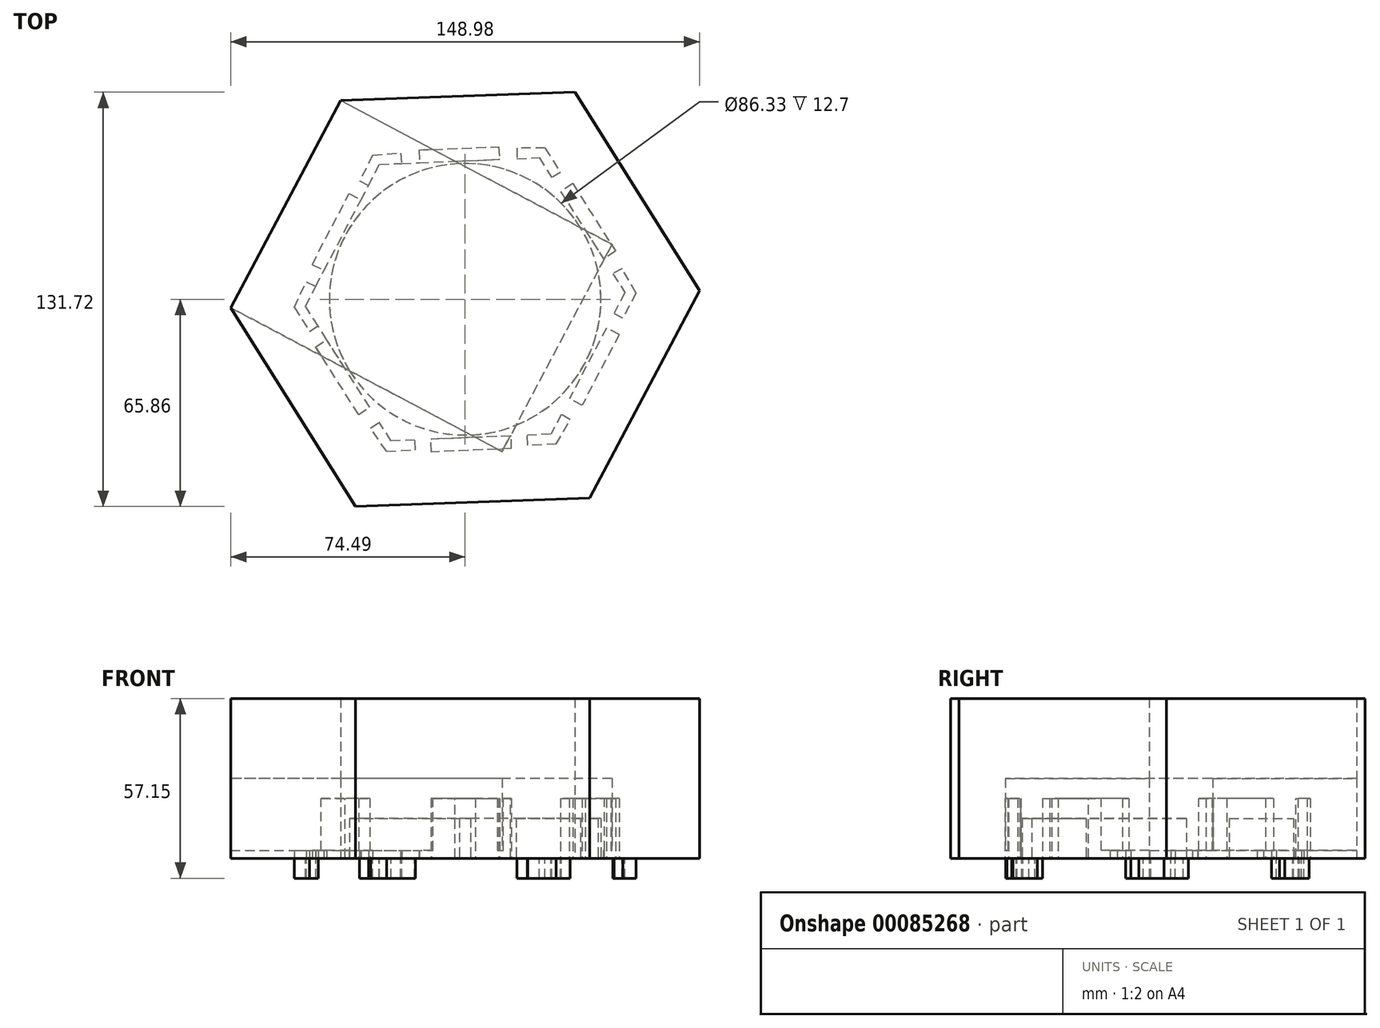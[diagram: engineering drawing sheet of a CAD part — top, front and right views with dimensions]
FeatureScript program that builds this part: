
annotation { "Feature Type Name" : "Feature", "Feature Type Description" : "" }
export const myFeature = defineFeature(function(context is Context, id is Id, definition is map)
    precondition{}
    {
        {
            var Q0;
            Q0=qCreatedBy(makeId("Top.planeOp"),FACE);
            var sketch = newSketch(context, id + "F0", { "sketchPlane" : qUnion([Q0])});
            skLineSegment(sketch, "E0.0", {"start": v(74.5, 2.7) * mm, "end": v(39.58, -63.16) * mm});
            skLineSegment(sketch, "E0.1", {"start": v(39.58, -63.16) * mm, "end": v(-34.9, -65.86) * mm});
            skLineSegment(sketch, "E0.2", {"start": v(-34.9, -65.86) * mm, "end": v(-74.5, -2.7) * mm});
            skLineSegment(sketch, "E0.3", {"start": v(-74.5, -2.7) * mm, "end": v(-39.58, 63.16) * mm});
            skLineSegment(sketch, "E0.4", {"start": v(-39.58, 63.16) * mm, "end": v(34.9, 65.86) * mm});
            skLineSegment(sketch, "E0.5", {"start": v(34.9, 65.86) * mm, "end": v(74.5, 2.7) * mm});
            skPoint(sketch, "E0.0.midPoint", {"position": v(57.04, -30.23) * mm});
            skCircle(sketch, "E1", {"center": v(0, 0) * mm, "radius": 64.56 * mm});
            skCircle(sketch, "E2", {"center": v(0, 0) * mm, "radius": 43.17 * mm});
            skSolve(sketch);
        }
        {
            var Q0;
            Q0=makeQuery(id+"F0.imprint","IMPRINT",FACE,{"disambiguationData":[TD([[makeQuery(id+"F0.imprint","IMPRINT",EDGE,{"derivedFrom":sQuery(id+"F0.wireOp",EDGE,"E0.0")}),-1.0]])]});
            var Q1;
            {var subQ0=sQuery(id+"F0.wireOp",EDGE,"E0.2");var subQ1=sQuery(id+"F0.wireOp",EDGE,"E0.1");var subQ2=makeQuery(id+"F0.imprint","INTERSECT",VERTEX,{"derivedFrom":[subQ1,subQ0]});Q1=makeQuery(id+"F0.imprint","IMPRINT",FACE,{"disambiguationData":[TD([[makeQuery(id+"F0.imprint","IMPRINT",EDGE,{"disambiguationData":[TD([[subQ2,1.0]])],"derivedFrom":subQ1}),-1.0]])]});}
            var Q2;
            {var subQ0=sQuery(id+"F0.wireOp",EDGE,"E0.3");var subQ1=sQuery(id+"F0.wireOp",EDGE,"E0.2");var subQ2=makeQuery(id+"F0.imprint","INTERSECT",VERTEX,{"derivedFrom":[subQ1,subQ0]});Q2=makeQuery(id+"F0.imprint","IMPRINT",FACE,{"disambiguationData":[TD([[makeQuery(id+"F0.imprint","IMPRINT",EDGE,{"disambiguationData":[TD([[subQ2,1.0]])],"derivedFrom":subQ1}),-1.0]])]});}
            var Q3;
            {var subQ0=sQuery(id+"F0.wireOp",EDGE,"E1");var subQ4=makeQuery(id+"F0.imprint","INTERSECT",VERTEX,{"derivedFrom":[sQuery(id+"F0.wireOp",EDGE,"E0.4"),subQ0]});Q3=makeQuery(id+"F0.imprint","IMPRINT",FACE,{"disambiguationData":[TD([[makeQuery(id+"F0.imprint","IMPRINT",EDGE,{"disambiguationData":[TD([[subQ4,1.0]])],"derivedFrom":subQ0}),1.0]])]});}
            var Q4;
            {var subQ0=sQuery(id+"F0.wireOp",EDGE,"E0.4");var subQ1=sQuery(id+"F0.wireOp",EDGE,"E0.3");var subQ2=makeQuery(id+"F0.imprint","INTERSECT",VERTEX,{"derivedFrom":[subQ1,subQ0]});Q4=makeQuery(id+"F0.imprint","IMPRINT",FACE,{"disambiguationData":[TD([[makeQuery(id+"F0.imprint","IMPRINT",EDGE,{"disambiguationData":[TD([[subQ2,1.0]])],"derivedFrom":subQ1}),-1.0]])]});}
            var Q5;
            {var subQ0=sQuery(id+"F0.wireOp",EDGE,"E0.5");var subQ1=sQuery(id+"F0.wireOp",EDGE,"E0.4");var subQ2=makeQuery(id+"F0.imprint","INTERSECT",VERTEX,{"derivedFrom":[subQ1,subQ0]});Q5=makeQuery(id+"F0.imprint","IMPRINT",FACE,{"disambiguationData":[TD([[makeQuery(id+"F0.imprint","IMPRINT",EDGE,{"disambiguationData":[TD([[subQ2,1.0]])],"derivedFrom":subQ1}),-1.0]])]});}
            var Q6;
            Q6=makeQuery(id+"F0.imprint","IMPRINT",FACE,{"disambiguationData":[TD([[makeQuery(id+"F0.imprint","IMPRINT",EDGE,{"derivedFrom":sQuery(id+"F0.wireOp",EDGE,"E2")}),1.0]])]});
            extrude(context, id + "F1", {"entities" : qUnion([Q0, Q1, Q2, Q3, Q4, Q5, Q6]), "depth" : 50.8 * mm});
        }
        {
            var Q0;
            Q0=makeQuery(id+"F0.imprint","IMPRINT",FACE,{"disambiguationData":[TD([[makeQuery(id+"F0.imprint","IMPRINT",EDGE,{"derivedFrom":sQuery(id+"F0.wireOp",EDGE,"E2")}),1.0]])]});
            extrude(context, id + "F2", {"entities" : qUnion([Q0]), "operationType" : NewBodyOperationType.REMOVE, "depth" : 12.7 * mm});
        }
        {
            var Q0;
            Q0=makeQuery(id+"F1.opExtrude","SWEPT_FACE",FACE,{"disambiguationData":[OSD([sQuery(id+"F0.wireOp",EDGE,"E0.3")])]});
            var sketch = newSketch(context, id + "F3", { "sketchPlane" : qUnion([Q0])});
            skLineSegment(sketch, "E3.bottom", {"start": v(-37.27, 25.4) * mm, "end": v(37.27, 25.4) * mm});
            skLineSegment(sketch, "E3.top", {"start": v(-37.27, 0.14) * mm, "end": v(37.27, 0.14) * mm});
            skLineSegment(sketch, "E3.left", {"start": v(-37.27, 25.4) * mm, "end": v(-37.27, 0.14) * mm});
            skLineSegment(sketch, "E3.right", {"start": v(37.27, 25.4) * mm, "end": v(37.27, 0.14) * mm});
            skPoint(sketch, "E3.middle", {"position": v(0, 12.77) * mm});
            skSolve(sketch);
        }
        {
            var Q0;
            Q0=makeQuery(id+"F0.imprint","IMPRINT",FACE,{"disambiguationData":[TD([[makeQuery(id+"F0.imprint","IMPRINT",EDGE,{"derivedFrom":sQuery(id+"F0.wireOp",EDGE,"E2")}),-1.0]])]});
            var sketch = newSketch(context, id + "F4", { "sketchPlane" : qUnion([Q0])});
            skLineSegment(sketch, "E4.0", {"start": v(-23.53, -45.02) * mm, "end": v(-50.76, -2.14) * mm});
            skLineSegment(sketch, "E4.1", {"start": v(-50.76, -2.14) * mm, "end": v(-27.23, 42.89) * mm});
            skLineSegment(sketch, "E4.2", {"start": v(-27.23, 42.89) * mm, "end": v(23.53, 45.02) * mm});
            skLineSegment(sketch, "E4.3", {"start": v(23.53, 45.02) * mm, "end": v(50.76, 2.14) * mm});
            skLineSegment(sketch, "E4.4", {"start": v(50.76, 2.14) * mm, "end": v(27.23, -42.89) * mm});
            skLineSegment(sketch, "E4.5", {"start": v(27.23, -42.89) * mm, "end": v(-23.53, -45.02) * mm});
            skPoint(sketch, "E4.0.midPoint", {"position": v(-37.14, -23.58) * mm});
            skLineSegment(sketch, "E5", {"start": v(2.02, -47.96) * mm, "end": v(-10.67, -48.5) * mm});
            skLineSegment(sketch, "E6", {"start": v(-10.67, -48.5) * mm, "end": v(-10.84, -44.49) * mm});
            skLineSegment(sketch, "E7", {"start": v(-10.84, -44.49) * mm, "end": v(14.7, -43.41) * mm});
            skLineSegment(sketch, "E8", {"start": v(2.02, -47.96) * mm, "end": v(14.7, -47.43) * mm});
            skLineSegment(sketch, "E9", {"start": v(14.7, -47.43) * mm, "end": v(14.7, -43.41) * mm});
            skLineSegment(sketch, "E10", {"start": v(43.03, -22.48) * mm, "end": v(48.91, -11.23) * mm});
            skLineSegment(sketch, "E11", {"start": v(48.91, -11.23) * mm, "end": v(44.87, -9.12) * mm});
            skLineSegment(sketch, "E12", {"start": v(43.03, -22.48) * mm, "end": v(37.15, -33.74) * mm});
            skLineSegment(sketch, "E13", {"start": v(37.15, -33.74) * mm, "end": v(33.11, -31.63) * mm});
            skLineSegment(sketch, "E14", {"start": v(-40.7, -25.84) * mm, "end": v(-33.9, -36.56) * mm});
            skLineSegment(sketch, "E15", {"start": v(-33.9, -36.56) * mm, "end": v(-30.33, -34.3) * mm});
            skLineSegment(sketch, "E16", {"start": v(-40.7, -25.84) * mm, "end": v(-47.51, -15.12) * mm});
            skLineSegment(sketch, "E17", {"start": v(-47.51, -15.12) * mm, "end": v(-43.95, -12.86) * mm});
            skPoint(sketch, "E18.start.orphan", {"position": v(39, -20.37) * mm});
            skPoint(sketch, "E19.end.orphan", {"position": v(1.85, -43.96) * mm});
            skLineSegment(sketch, "E20.MirrorCS", {"start": v(-36.85, 33.58) * mm, "end": v(-33.11, 31.63) * mm});
            skLineSegment(sketch, "E21.MirrorCS", {"start": v(-42.73, 22.33) * mm, "end": v(-36.85, 33.58) * mm});
            skLineSegment(sketch, "E22.MirrorCS", {"start": v(-42.73, 22.33) * mm, "end": v(-48.61, 11.07) * mm});
            skLineSegment(sketch, "E23.MirrorCS", {"start": v(-48.61, 11.07) * mm, "end": v(-44.87, 9.12) * mm});
            skLineSegment(sketch, "E24.MirrorCS", {"start": v(-2.02, 47.96) * mm, "end": v(10.67, 48.5) * mm});
            skLineSegment(sketch, "E25.MirrorCS", {"start": v(-14.7, 47.43) * mm, "end": v(-14.54, 43.42) * mm});
            skLineSegment(sketch, "E26.MirrorCS", {"start": v(10.67, 48.5) * mm, "end": v(11, 44.5) * mm});
            skLineSegment(sketch, "E27.MirrorCS", {"start": v(-2.02, 47.96) * mm, "end": v(-14.7, 47.43) * mm});
            skLineSegment(sketch, "E28.MirrorCS", {"start": v(40.99, 26.02) * mm, "end": v(34.18, 36.74) * mm});
            skLineSegment(sketch, "E29.MirrorCS", {"start": v(40.99, 26.02) * mm, "end": v(47.8, 15.3) * mm});
            skLineSegment(sketch, "E30.MirrorCS", {"start": v(34.18, 36.74) * mm, "end": v(30.33, 34.3) * mm});
            skLineSegment(sketch, "E31.MirrorCS", {"start": v(47.8, 15.3) * mm, "end": v(43.95, 12.86) * mm});
            skLineSegment(sketch, "E32", {"start": v(25.4, 48.06) * mm, "end": v(30.27, 40.38) * mm});
            skLineSegment(sketch, "E33", {"start": v(30.27, 40.38) * mm, "end": v(27.57, 38.66) * mm});
            skLineSegment(sketch, "E34", {"start": v(25.4, 48.06) * mm, "end": v(16.45, 48.06) * mm});
            skLineSegment(sketch, "E35", {"start": v(16.45, 48.06) * mm, "end": v(16.45, 44.73) * mm});
            skLineSegment(sketch, "E36.MirrorCS", {"start": v(-30.06, -40.95) * mm, "end": v(-27.32, -39.05) * mm});
            skLineSegment(sketch, "E37.MirrorCS", {"start": v(-24.95, -48.29) * mm, "end": v(-30.06, -40.95) * mm});
            skLineSegment(sketch, "E38.MirrorCS", {"start": v(-24.95, -48.29) * mm, "end": v(-15.86, -47.9) * mm});
            skLineSegment(sketch, "E39.MirrorCS", {"start": v(-15.86, -47.9) * mm, "end": v(-16, -44.7) * mm});
            skLineSegment(sketch, "E40.MirrorCS", {"start": v(28.93, -46.02) * mm, "end": v(19.83, -46.4) * mm});
            skLineSegment(sketch, "E41.MirrorCS", {"start": v(28.93, -46.02) * mm, "end": v(33.4, -38.28) * mm});
            skLineSegment(sketch, "E42.MirrorCS", {"start": v(33.4, -38.28) * mm, "end": v(30.5, -36.61) * mm});
            skLineSegment(sketch, "E43.MirrorCS", {"start": v(19.83, -46.4) * mm, "end": v(19.7, -43.2) * mm});
            skPoint(sketch, "E44.end.orphan", {"position": v(37.14, 23.58) * mm});
            skPoint(sketch, "E45.orphan", {"position": v(-1.85, 43.96) * mm});
            skPoint(sketch, "E46.orphan", {"position": v(-39, 20.37) * mm});
            skLineSegment(sketch, "E47.MirrorCS", {"start": v(54.32, 2.04) * mm, "end": v(49.85, 9.78) * mm});
            skLineSegment(sketch, "E48.MirrorCS", {"start": v(54.32, 2.04) * mm, "end": v(50.1, -6.03) * mm});
            skLineSegment(sketch, "E49.MirrorCS", {"start": v(49.85, 9.78) * mm, "end": v(46.96, 8.11) * mm});
            skLineSegment(sketch, "E50.MirrorCS", {"start": v(50.1, -6.03) * mm, "end": v(47.26, -4.54) * mm});
            skLineSegment(sketch, "E51.MirrorCS", {"start": v(-50.5, 5.55) * mm, "end": v(-47.48, 4.14) * mm});
            skLineSegment(sketch, "E52.MirrorCS", {"start": v(-54.3, -2.53) * mm, "end": v(-50.5, 5.55) * mm});
            skLineSegment(sketch, "E53.MirrorCS", {"start": v(-50.76, -2.14) * mm, "end": v(-23.53, -45.02) * mm});
            skLineSegment(sketch, "E54.MirrorCS", {"start": v(-54.3, -2.53) * mm, "end": v(-49.42, -10.22) * mm});
            skLineSegment(sketch, "E55.MirrorCS", {"start": v(-49.42, -10.22) * mm, "end": v(-46.72, -8.5) * mm});
            skLineSegment(sketch, "E56.MirrorCS", {"start": v(-29.34, 45.75) * mm, "end": v(-20.44, 46.5) * mm});
            skLineSegment(sketch, "E57.MirrorCS", {"start": v(-29.34, 45.75) * mm, "end": v(-33.56, 37.69) * mm});
            skLineSegment(sketch, "E58.MirrorCS", {"start": v(-33.56, 37.69) * mm, "end": v(-30.72, 36.2) * mm});
            skLineSegment(sketch, "E59.MirrorCS", {"start": v(-20.44, 46.5) * mm, "end": v(-20.16, 43.18) * mm});
            skSolve(sketch);
        }
        {
            var Q0;
            Q0=makeQuery(id+"F3.imprint","IMPRINT",FACE,{"disambiguationData":[TD([[makeQuery(id+"F3.imprint","IMPRINT",EDGE,{"derivedFrom":sQuery(id+"F3.wireOp",EDGE,"E3.bottom")}),-1.0]])]});
            var Q1;
            Q1=sQuery(id+"F3.wireOp",EDGE,"E3.right");
            var Q2;
            Q2=sQuery(id+"F3.wireOp",EDGE,"E3.bottom");
            var Q3;
            Q3=sQuery(id+"F3.wireOp",EDGE,"E3.left");
            var Q4;
            Q4=sQuery(id+"F3.wireOp",EDGE,"E3.top");
            extrude(context, id + "F5", {"entities" : qUnion([Q0]), "operationType" : NewBodyOperationType.REMOVE, "surfaceEntities" : qUnion([Q1, Q2, Q3, Q4]), "oppositeDirection" : true, "depth" : 97.6 * mm});
        }
        {
            var Q0;
            Q0=makeQuery(id+"F4.imprint","IMPRINT",FACE,{"disambiguationData":[TD([[makeQuery(id+"F4.imprint","IMPRINT",EDGE,{"derivedFrom":sQuery(id+"F4.wireOp",EDGE,"E5")}),-1.0]])]});
            var Q1;
            Q1=makeQuery(id+"F4.imprint","IMPRINT",FACE,{"disambiguationData":[TD([[makeQuery(id+"F4.imprint","IMPRINT",EDGE,{"derivedFrom":sQuery(id+"F4.wireOp",EDGE,"E28.MirrorCS")}),1.0]])]});
            var Q2;
            Q2=makeQuery(id+"F4.imprint","IMPRINT",FACE,{"disambiguationData":[TD([[makeQuery(id+"F4.imprint","IMPRINT",EDGE,{"derivedFrom":sQuery(id+"F4.wireOp",EDGE,"E10")}),1.0]])]});
            extrude(context, id + "F6", {"entities" : qUnion([Q0, Q1, Q2]), "operationType" : NewBodyOperationType.REMOVE, "depth" : 19.05 * mm});
        }
        {
            var Q0;
            Q0=makeQuery(id+"F4.imprint","IMPRINT",FACE,{"disambiguationData":[TD([[makeQuery(id+"F4.imprint","IMPRINT",EDGE,{"derivedFrom":sQuery(id+"F4.wireOp",EDGE,"E14")}),1.0]])]});
            var Q1;
            {var subQ0=sQuery(id+"F4.wireOp",EDGE,"E20.MirrorCS");Q1=makeQuery(id+"F4.imprint","IMPRINT",FACE,{"disambiguationData":[TD([[makeQuery(id+"F4.imprint","IMPRINT",EDGE,{"derivedFrom":subQ0}),-1.0]])]});}
            var Q2;
            {var subQ1=sQuery(id+"F4.wireOp",EDGE,"E25.MirrorCS");Q2=makeQuery(id+"F4.imprint","IMPRINT",FACE,{"disambiguationData":[TD([[makeQuery(id+"F4.imprint","IMPRINT",EDGE,{"derivedFrom":subQ1}),1.0]])]});}
            extrude(context, id + "F7", {"entities" : qUnion([Q0, Q1, Q2]), "operationType" : NewBodyOperationType.REMOVE, "depth" : 19.05 * mm});
        }
        {
            var Q0;
            {var subQ0=sQuery(id+"F0.wireOp",EDGE,"E0.4");var subQ1=sQuery(id+"F0.wireOp",EDGE,"E0.3");var subQ2=makeQuery(id+"F0.imprint","INTERSECT",VERTEX,{"derivedFrom":[subQ1,subQ0]});Q0=makeQuery(id+"F0.imprint","IMPRINT",FACE,{"disambiguationData":[TD([[makeQuery(id+"F0.imprint","IMPRINT",EDGE,{"disambiguationData":[TD([[subQ2,1.0]])],"derivedFrom":subQ1}),-1.0]])]});}
            var Q1;
            Q1=makeQuery(id+"F4.imprint","IMPRINT",FACE,{"disambiguationData":[TD([[makeQuery(id+"F4.imprint","IMPRINT",EDGE,{"derivedFrom":sQuery(id+"F4.wireOp",EDGE,"E5")}),1.0]])]});
            var Q2;
            {var subQ0=sQuery(id+"F0.wireOp",EDGE,"E0.3");var subQ1=sQuery(id+"F0.wireOp",EDGE,"E0.2");var subQ2=makeQuery(id+"F0.imprint","INTERSECT",VERTEX,{"derivedFrom":[subQ1,subQ0]});Q2=makeQuery(id+"F0.imprint","IMPRINT",FACE,{"disambiguationData":[TD([[makeQuery(id+"F0.imprint","IMPRINT",EDGE,{"disambiguationData":[TD([[subQ2,1.0]])],"derivedFrom":subQ1}),-1.0]])]});}
            extrude(context, id + "F8", {"entities" : qUnion([Q0, Q1, Q2]), "operationType" : NewBodyOperationType.ADD, "depth" : 2.54 * mm});
        }
        {
            var Q0;
            {var subQ0=sQuery(id+"F4.wireOp",EDGE,"E42.MirrorCS");Q0=makeQuery(id+"F4.imprint","IMPRINT",FACE,{"disambiguationData":[TD([[makeQuery(id+"F4.imprint","IMPRINT",EDGE,{"derivedFrom":subQ0}),1.0]])]});}
            var Q1;
            {var subQ0=sQuery(id+"F4.wireOp",EDGE,"E39.MirrorCS");Q1=makeQuery(id+"F4.imprint","IMPRINT",FACE,{"disambiguationData":[TD([[makeQuery(id+"F4.imprint","IMPRINT",EDGE,{"derivedFrom":subQ0}),1.0]])]});}
            var Q2;
            {var subQ4=sQuery(id+"F4.wireOp",EDGE,"E51.MirrorCS");Q2=makeQuery(id+"F4.imprint","IMPRINT",FACE,{"disambiguationData":[TD([[makeQuery(id+"F4.imprint","IMPRINT",EDGE,{"derivedFrom":subQ4}),-1.0]])]});}
            var Q3;
            Q3=makeQuery(id+"F4.imprint","IMPRINT",FACE,{"disambiguationData":[TD([[makeQuery(id+"F4.imprint","IMPRINT",EDGE,{"derivedFrom":sQuery(id+"F4.wireOp",EDGE,"E56.MirrorCS")}),-1.0]])]});
            var Q4;
            Q4=makeQuery(id+"F4.imprint","IMPRINT",FACE,{"disambiguationData":[TD([[makeQuery(id+"F4.imprint","IMPRINT",EDGE,{"derivedFrom":sQuery(id+"F4.wireOp",EDGE,"E32")}),-1.0]])]});
            var Q5;
            Q5=makeQuery(id+"F4.imprint","IMPRINT",FACE,{"disambiguationData":[TD([[makeQuery(id+"F4.imprint","IMPRINT",EDGE,{"derivedFrom":sQuery(id+"F4.wireOp",EDGE,"E47.MirrorCS")}),1.0]])]});
            extrude(context, id + "F9", {"entities" : qUnion([Q0, Q1, Q2, Q3, Q4, Q5]), "operationType" : NewBodyOperationType.ADD, "oppositeDirection" : true, "depth" : 6.35 * mm});
        }
    });
